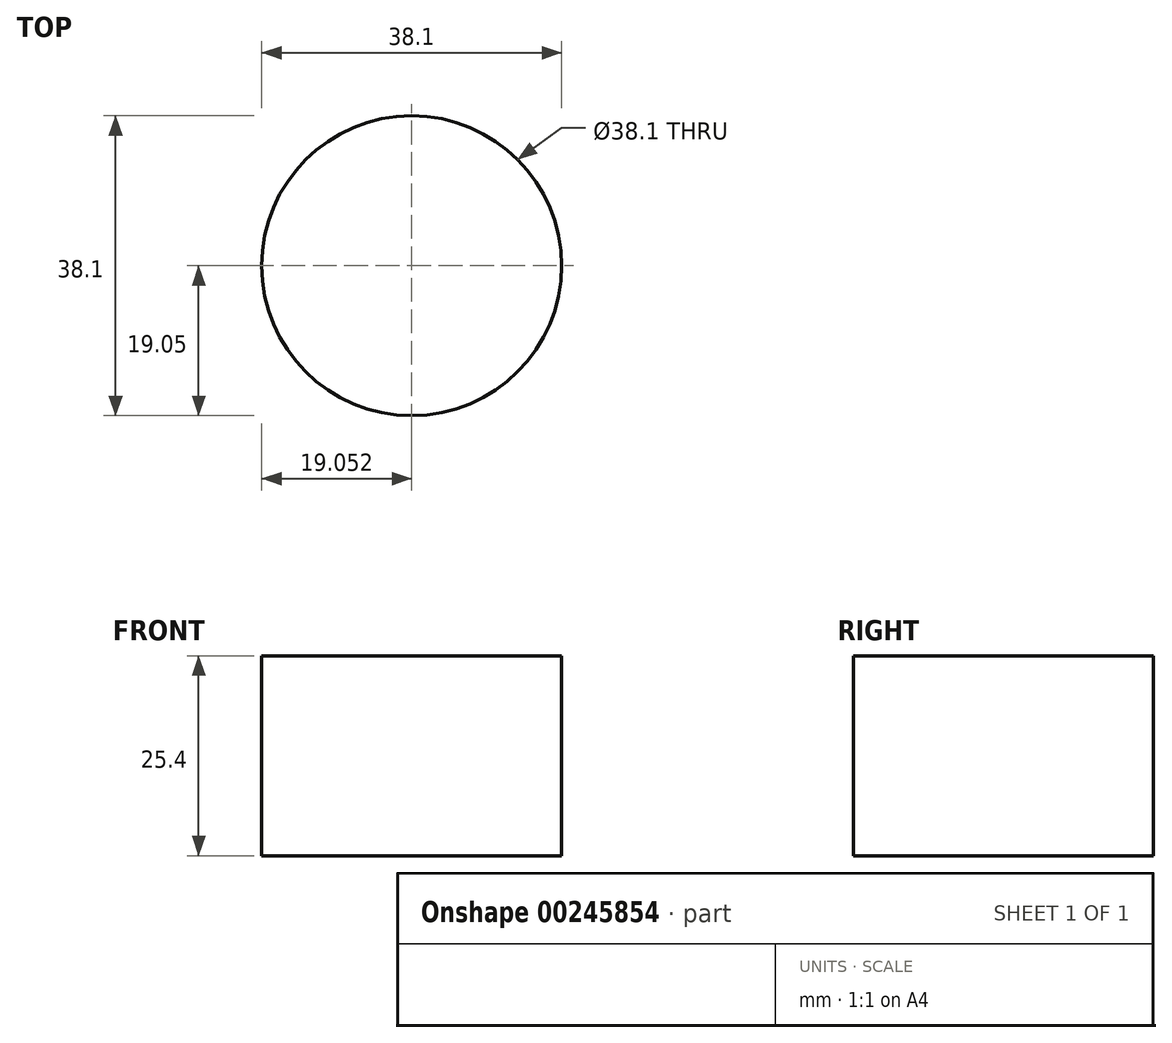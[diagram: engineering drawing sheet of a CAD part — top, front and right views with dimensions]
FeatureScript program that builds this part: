
annotation { "Feature Type Name" : "Feature", "Feature Type Description" : "" }
export const myFeature = defineFeature(function(context is Context, id is Id, definition is map)
    precondition{}
    {
        {
            var Q0;
            Q0=qCreatedBy(makeId("Top.planeOp"),FACE);
            var sketch = newSketch(context, id + "F0", { "sketchPlane" : qUnion([Q0])});
            skCircle(sketch, "E0", {"center": v(52.12, 0) * mm, "radius": 19.05 * mm});
            skSolve(sketch);
        }
        {
            var Q0;
            Q0=sQuery(id+"F0.wireOp",EDGE,"E0");
            extrude(context, id + "F1", {"bodyType" : ToolBodyType.SURFACE, "surfaceEntities" : qUnion([Q0]), "oppositeDirection" : true, "depth" : 25.4 * mm});
        }
    });
